# Revit family: Access_Door_ACUDOR_FireRated_Uninsulated_Tile_FB-5060-TD
name_source: partatom
category: Doors
revit_build: Autodesk Revit 2017 (Build: 20171027_0315(x64)
units: mm (PartAtom-declared; Revit-internal decimal feet)

## family parameters
Cut with Voids When Loaded = No
Host = Face
Room Calculation Point = No
Shared = No

## types (7) — shared parameters
Analytic Construction = <None>
Default Elevation = 48 "
Description = RECESSED FOR TILE FIRE RETED - FOR WALLS
Manufacturer = ACUDOR
Material Finish = Metal - Acudor - Stainless - Polished
URL = www.acudor.com
zero-valued in all types: Thickness

## per-type parameters (varying)
| type | Code | Height | Wall Offset | Width |
| FB-5060-TD-0808 | 1 | 10 " | 0.5 " | 10 " |
| FB-5060-TD-1010 | 2 | 12 " | 0 " | 12 " |
| FB-5060-TD-1414 | 4 | 16 " | 0 " | 16 " |
| FB-5060-TD-1616 | 5 | 18 " | 0 " | 18 " |
| FB-5060-TD-1818 | 6 | 20 " | 0 " | 20 " |
| FB-5060-TD-1212 | 3 | 14 " | 0 " | 14 " |
| FB-5060-TD-2424 | 6 | 26 " | 0 " | 26 " |

note: column(s) folded — value = type name in every type: Model

## geometry (parser evidence)
native form markers: Blend x4, Sweep x12
no freeform markers — native parametric forms only
